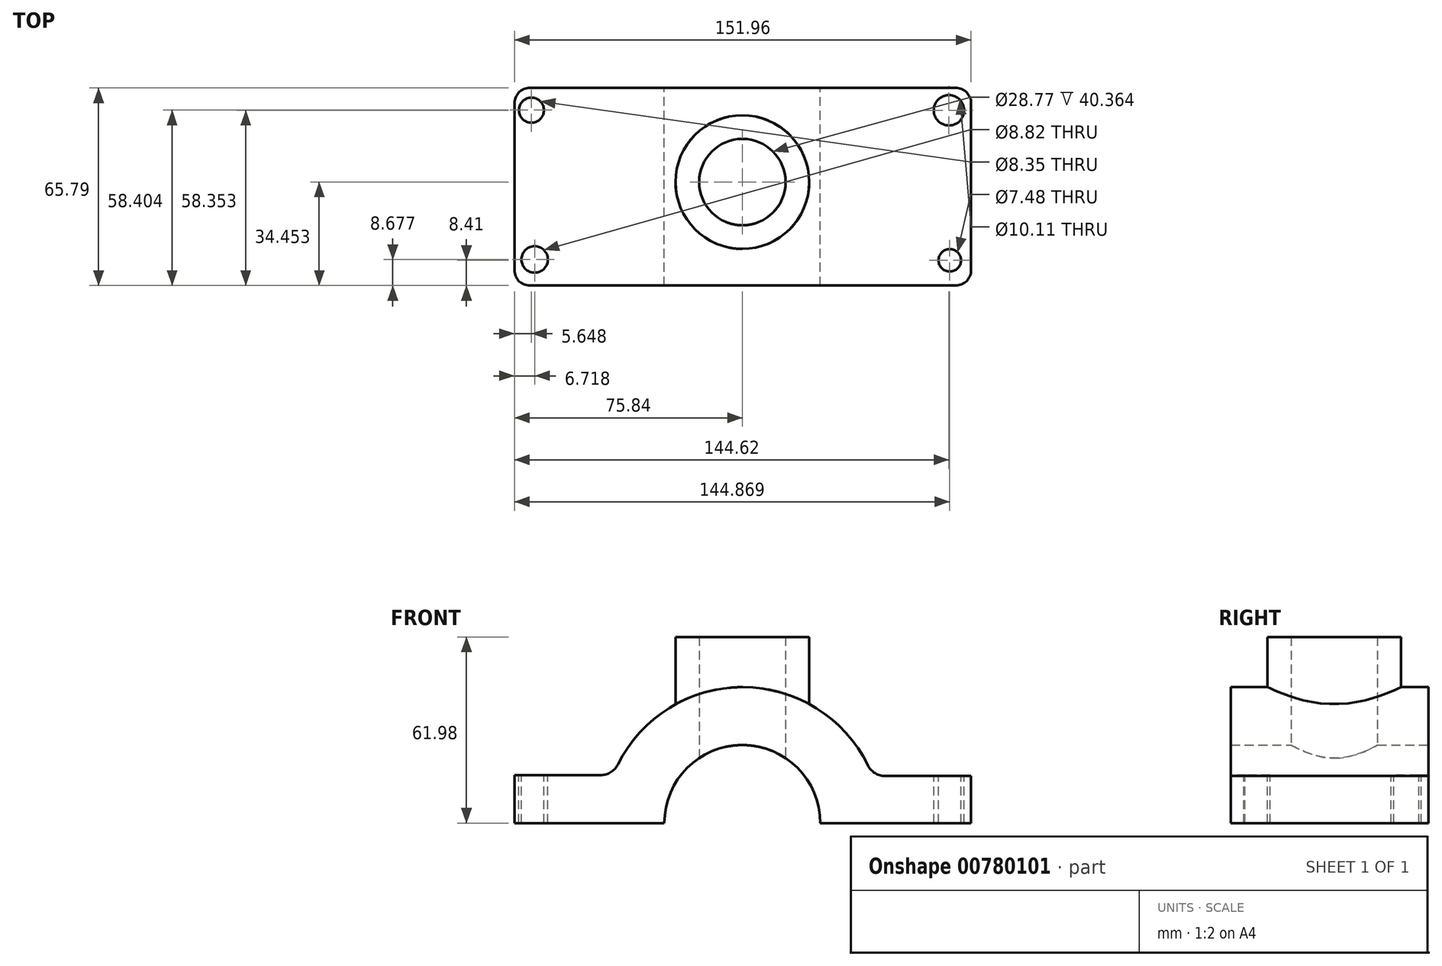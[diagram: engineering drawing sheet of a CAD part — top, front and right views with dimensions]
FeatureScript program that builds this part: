
annotation { "Feature Type Name" : "Feature", "Feature Type Description" : "" }
export const myFeature = defineFeature(function(context is Context, id is Id, definition is map)
    precondition{}
    {
        {
            var Q0;
            Q0=qCreatedBy(makeId("Front.planeOp"),FACE);
            var sketch = newSketch(context, id + "F0", { "sketchPlane" : qUnion([Q0])});
            skArc(sketch, "E0", {"start": v(25.79, 0) * mm, "mid": v(0, 25.79) * mm, "end": v(-25.79, 0) * mm});
            skLineSegment(sketch, "E1", {"start": v(0, 0) * mm, "end": v(-25.79, 0) * mm, "construction": true});
            skLineSegment(sketch, "E2", {"start": v(-25.79, 0) * mm, "end": v(25.79, 0) * mm, "construction": true});
            skLineSegment(sketch, "E3", {"start": v(-25.79, 0) * mm, "end": v(-75.84, 0) * mm});
            skLineSegment(sketch, "E4", {"start": v(25.79, 0) * mm, "end": v(76.12, 0) * mm});
            skLineSegment(sketch, "E5", {"start": v(-75.84, 0) * mm, "end": v(-75.84, 15.97) * mm});
            skLineSegment(sketch, "E6", {"start": v(76.12, 0) * mm, "end": v(76.12, 15.69) * mm});
            skLineSegment(sketch, "E7", {"start": v(76.12, 15.69) * mm, "end": v(47.46, 15.69) * mm});
            skLineSegment(sketch, "E8", {"start": v(-75.84, 15.97) * mm, "end": v(-47.14, 15.97) * mm});
            skArc(sketch, "E9", {"start": v(41.76, 19.25) * mm, "mid": v(0.23, 45.26) * mm, "end": v(-41.46, 19.5) * mm});
            skPoint(sketch, "E10.visualSharp", {"position": v(-43.03, 15.97) * mm});
            skArc(sketch, "E10.filletArc", {"start": v(-47.14, 15.97) * mm, "mid": v(-43.8, 16.93) * mm, "end": v(-41.46, 19.5) * mm});
            skPoint(sketch, "E11.visualSharp", {"position": v(43.31, 15.69) * mm});
            skArc(sketch, "E11.filletArc", {"start": v(41.76, 19.25) * mm, "mid": v(44.1, 16.65) * mm, "end": v(47.46, 15.69) * mm});
            skSolve(sketch);
        }
        {
            var Q0;
            Q0=makeQuery(id+"F0.imprint","IMPRINT",FACE,{"disambiguationData":[TD([[makeQuery(id+"F0.imprint","IMPRINT",EDGE,{"derivedFrom":sQuery(id+"F0.wireOp",EDGE,"E0")}),-1.0]])]});
            var Q1;
            {var subQ0=sQuery(id+"F0.wireOp",EDGE,"DLsdQfVf-2zxM-Xayb-AtiC-HBehDzJQTrXj");Q1=makeQuery(id+"F0.imprint","IMPRINT",FACE,{"disambiguationData":[TD([[makeQuery(id+"F0.imprint","IMPRINT",EDGE,{"derivedFrom":subQ0}),-1.0]])]});}
            extrude(context, id + "F1", {"entities" : qUnion([Q0, Q1]), "depth" : 65.8 * mm, "offsetDistance" : 25.4 * mm});
        }
        {
            var Q0;
            Q0=makeQuery(id+"F1.opExtrude","SWEPT_FACE",FACE,{"disambiguationData":[OSD([sQuery(id+"F0.wireOp",EDGE,"E8")])]});
            var sketch = newSketch(context, id + "F2", { "sketchPlane" : qUnion([Q0])});
            skCircle(sketch, "E12", {"center": v(-70.2, -7.39) * mm, "radius": 4.18 * mm});
            skCircle(sketch, "E13", {"center": v(-69.12, -57.11) * mm, "radius": 4.4 * mm});
            skCircle(sketch, "E14", {"center": v(68.78, -7.44) * mm, "radius": 5.06 * mm});
            skCircle(sketch, "E15", {"center": v(69.03, -57.38) * mm, "radius": 3.74 * mm});
            skSolve(sketch);
        }
        {
            var Q0;
            Q0=makeQuery(id+"F2.imprint","IMPRINT",FACE,{"disambiguationData":[TD([[makeQuery(id+"F2.imprint","IMPRINT",EDGE,{"derivedFrom":sQuery(id+"F2.wireOp",EDGE,"E12")}),1.0]])]});
            var Q1;
            Q1=makeQuery(id+"F2.imprint","IMPRINT",FACE,{"disambiguationData":[TD([[makeQuery(id+"F2.imprint","IMPRINT",EDGE,{"derivedFrom":sQuery(id+"F2.wireOp",EDGE,"E13")}),1.0]])]});
            extrude(context, id + "F3", {"entities" : qUnion([Q0, Q1]), "operationType" : NewBodyOperationType.REMOVE, "oppositeDirection" : true, "depth" : 25.4 * mm, "offsetDistance" : 25.4 * mm});
        }
        {
            var Q0;
            Q0=makeQuery(id+"F2.imprint","IMPRINT",FACE,{"disambiguationData":[TD([[makeQuery(id+"F2.imprint","IMPRINT",EDGE,{"derivedFrom":sQuery(id+"F2.wireOp",EDGE,"E14")}),1.0]])]});
            var Q1;
            Q1=makeQuery(id+"F2.imprint","IMPRINT",FACE,{"disambiguationData":[TD([[makeQuery(id+"F2.imprint","IMPRINT",EDGE,{"derivedFrom":sQuery(id+"F2.wireOp",EDGE,"E15")}),1.0]])]});
            extrude(context, id + "F4", {"entities" : qUnion([Q0, Q1]), "operationType" : NewBodyOperationType.REMOVE, "oppositeDirection" : true, "depth" : 25.4 * mm, "offsetDistance" : 25.4 * mm});
        }
        {
            var Q0;
            Q0=qCreatedBy(makeId("Top.planeOp"),FACE);
            var sketch = newSketch(context, id + "F5", { "sketchPlane" : qUnion([Q0])});
            skLineSegment(sketch, "E16", {"start": v(0, 0) * mm, "end": v(0, -87.21) * mm, "construction": true});
            skCircle(sketch, "E17", {"center": v(0, -31.34) * mm, "radius": 22.26 * mm});
            skCircle(sketch, "E18", {"center": v(0, -31.34) * mm, "radius": 14.39 * mm});
            skSolve(sketch);
        }
        {
            var Q0;
            Q0=makeQuery(id+"F5.imprint","IMPRINT",FACE,{"disambiguationData":[TD([[makeQuery(id+"F5.imprint","IMPRINT",EDGE,{"derivedFrom":sQuery(id+"F5.wireOp",EDGE,"E18")}),1.0]])]});
            extrude(context, id + "F6", {"entities" : qUnion([Q0]), "operationType" : NewBodyOperationType.REMOVE, "depth" : 68.07 * mm, "offsetDistance" : 25.4 * mm});
        }
        {
            var Q0;
            Q0=makeQuery(id+"F5.imprint","IMPRINT",FACE,{"disambiguationData":[TD([[makeQuery(id+"F5.imprint","IMPRINT",EDGE,{"derivedFrom":sQuery(id+"F5.wireOp",EDGE,"E17")}),1.0]])]});
            extrude(context, id + "F7", {"entities" : qUnion([Q0]), "operationType" : NewBodyOperationType.ADD, "depth" : 61.98 * mm, "offsetDistance" : 25.4 * mm});
        }
        {
            var Q0;
            Q0=makeQuery(id+"F1.opExtrude","CAP_EDGE",EDGE,{"disambiguationData":[OSD([sQuery(id+"F0.wireOp",EDGE,"E6")])],"isStart":false});
            var Q1;
            Q1=makeQuery(id+"F1.opExtrude","CAP_EDGE",EDGE,{"disambiguationData":[OSD([sQuery(id+"F0.wireOp",EDGE,"E6")])],"isStart":true});
            var Q2;
            Q2=makeQuery(id+"F1.opExtrude","CAP_EDGE",EDGE,{"disambiguationData":[OSD([sQuery(id+"F0.wireOp",EDGE,"E5")])],"isStart":true});
            var Q3;
            Q3=makeQuery(id+"F1.opExtrude","CAP_EDGE",EDGE,{"disambiguationData":[OSD([sQuery(id+"F0.wireOp",EDGE,"E5")])],"isStart":false});
            fillet(context, id + "F8", {"entities" : qUnion([Q0, Q1, Q2, Q3]), "radius" : 5.08 * mm, "tangentPropagation" : true, "allowEdgeOverflow" : false});
        }
        {
            var Q0;
            Q0=qCreatedBy(makeId("Front.planeOp"),FACE);
            var sketch = newSketch(context, id + "F9", { "sketchPlane" : qUnion([Q0])});
            skCircle(sketch, "E19", {"center": v(0, 0) * mm, "radius": 25.97 * mm});
            skSolve(sketch);
        }
        {
            var Q0;
            Q0=makeQuery(id+"F9.imprint","IMPRINT",FACE,{"disambiguationData":[TD([[makeQuery(id+"F9.imprint","IMPRINT",EDGE,{"derivedFrom":sQuery(id+"F9.wireOp",EDGE,"E19")}),1.0]])]});
            extrude(context, id + "F10", {"entities" : qUnion([Q0]), "operationType" : NewBodyOperationType.REMOVE, "depth" : 113.8 * mm, "offsetDistance" : 25.4 * mm});
        }
    });
